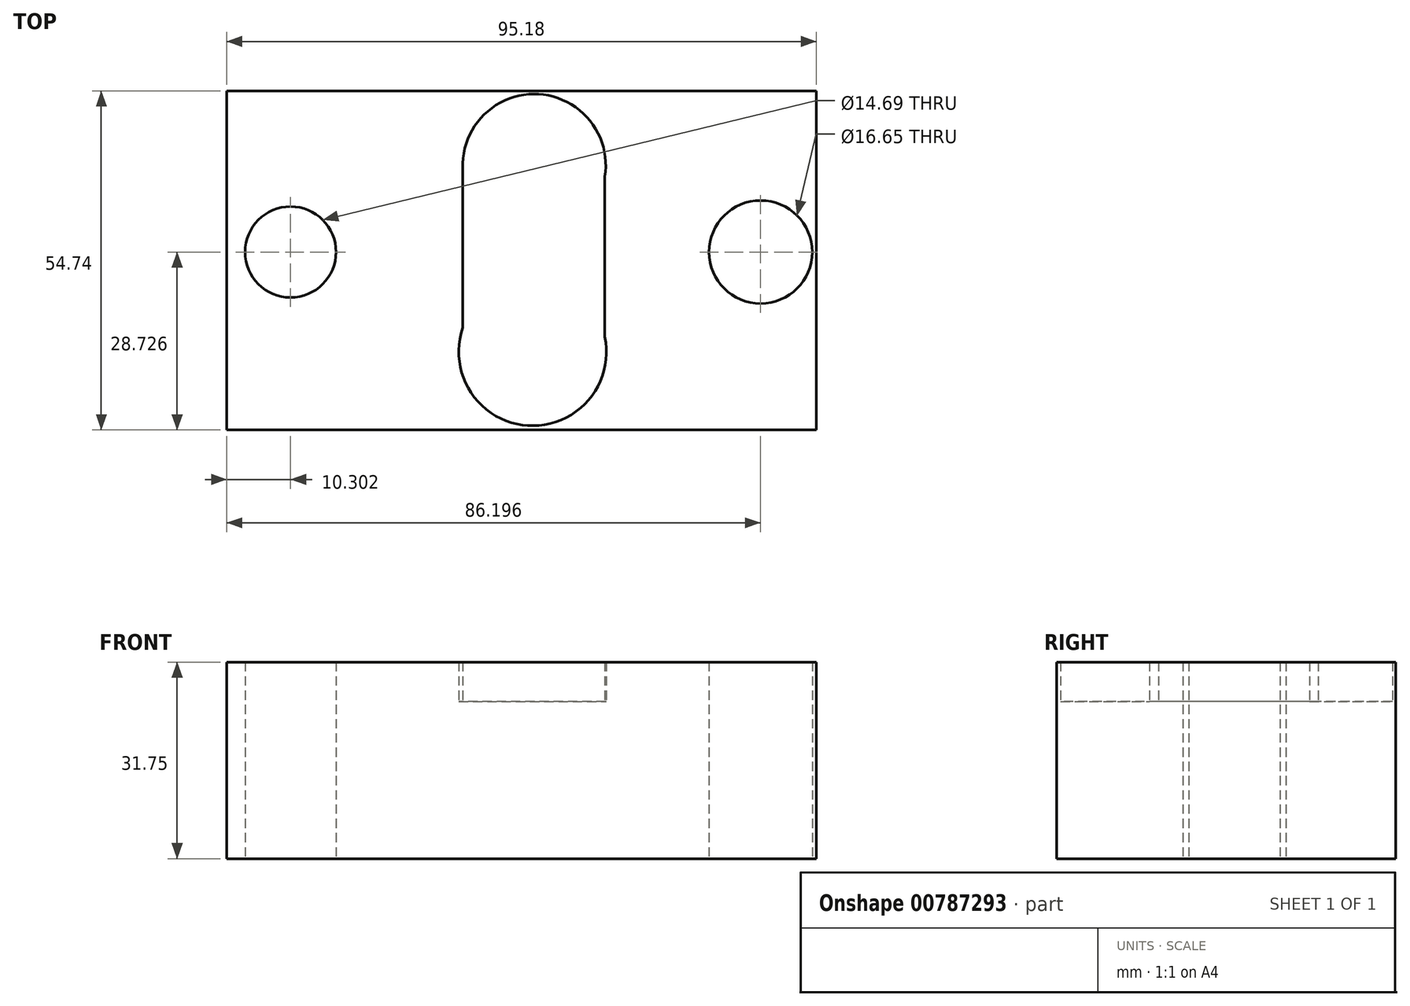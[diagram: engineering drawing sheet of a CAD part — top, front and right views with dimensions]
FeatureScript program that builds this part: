
annotation { "Feature Type Name" : "Feature", "Feature Type Description" : "" }
export const myFeature = defineFeature(function(context is Context, id is Id, definition is map)
    precondition{}
    {
        {
            var Q0;
            Q0=qCreatedBy(makeId("Top.planeOp"),FACE);
            var sketch = newSketch(context, id + "F0", { "sketchPlane" : qUnion([Q0])});
            skLineSegment(sketch, "E0.bottom", {"start": v(-46.94, 30.65) * mm, "end": v(48.24, 30.65) * mm});
            skLineSegment(sketch, "E0.top", {"start": v(-46.94, -24.1) * mm, "end": v(48.24, -24.1) * mm});
            skLineSegment(sketch, "E0.left", {"start": v(-46.94, 30.65) * mm, "end": v(-46.94, -24.1) * mm});
            skLineSegment(sketch, "E0.right", {"start": v(48.24, 30.65) * mm, "end": v(48.24, -24.1) * mm});
            skCircle(sketch, "E1", {"center": v(-36.64, 4.64) * mm, "radius": 7.34 * mm});
            skPoint(sketch, "E2.center.orphan", {"position": v(39.26, 4.64) * mm});
            skCircle(sketch, "E3", {"center": v(39.26, 4.64) * mm, "radius": 8.32 * mm});
            skArc(sketch, "E4", {"start": v(-8.81, -7.59) * mm, "mid": v(1.7, -23.39) * mm, "end": v(14.11, -9.05) * mm});
            skArc(sketch, "E5", {"start": v(14.11, 16.79) * mm, "mid": v(3.4, 30.13) * mm, "end": v(-8.81, 18.15) * mm});
            skLineSegment(sketch, "E6", {"start": v(-8.81, 18.15) * mm, "end": v(-8.81, -7.59) * mm});
            skLineSegment(sketch, "E7", {"start": v(14.11, 16.79) * mm, "end": v(14.11, -9.05) * mm});
            skSolve(sketch);
        }
        {
            var Q0;
            Q0=makeQuery(id+"F0.imprint","IMPRINT",FACE,{"disambiguationData":[TD([[makeQuery(id+"F0.imprint","IMPRINT",EDGE,{"derivedFrom":sQuery(id+"F0.wireOp",EDGE,"E0.bottom")}),-1.0]])]});
            extrude(context, id + "F1", {"entities" : qUnion([Q0]), "depth" : 31.75 * mm, "offsetDistance" : 25.4 * mm});
        }
        {
            var Q0;
            Q0=makeQuery(id+"F0.imprint","IMPRINT",FACE,{"disambiguationData":[TD([[makeQuery(id+"F0.imprint","IMPRINT",EDGE,{"derivedFrom":sQuery(id+"F0.wireOp",EDGE,"E4")}),1.0]])]});
            extrude(context, id + "F2", {"entities" : qUnion([Q0]), "operationType" : NewBodyOperationType.ADD, "depth" : 25.4 * mm, "offsetDistance" : 25.4 * mm});
        }
    });
